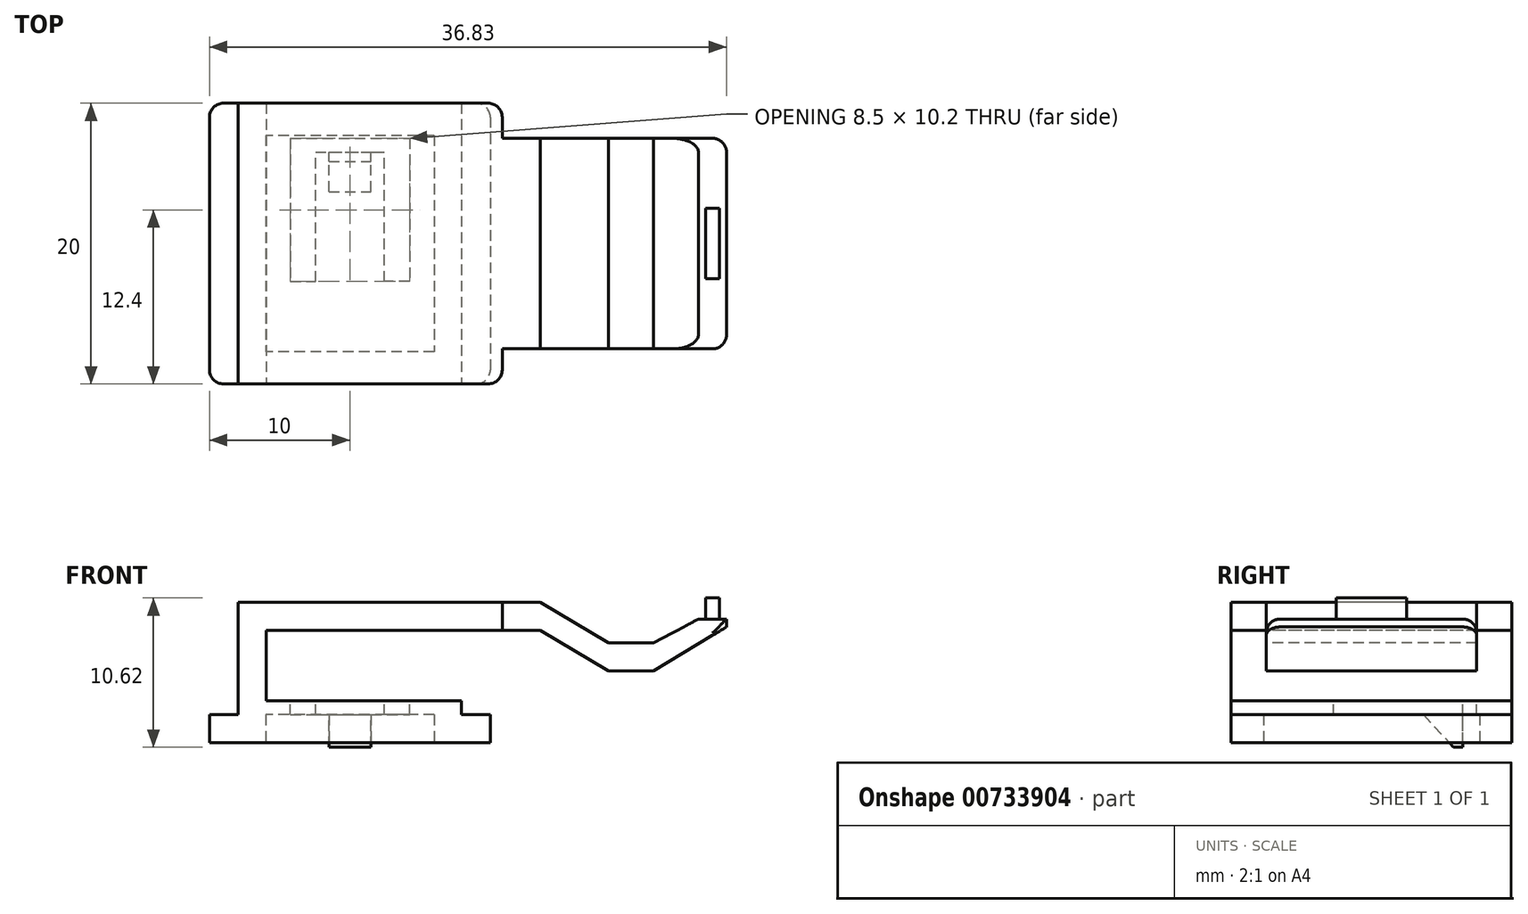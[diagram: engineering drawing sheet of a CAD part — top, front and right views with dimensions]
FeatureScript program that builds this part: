
annotation { "Feature Type Name" : "Feature", "Feature Type Description" : "" }
export const myFeature = defineFeature(function(context is Context, id is Id, definition is map)
    precondition{}
    {
        {
            var Q0;
            Q0=qCreatedBy(makeId("Top.planeOp"),FACE);
            var sketch = newSketch(context, id + "F0", { "sketchPlane" : qUnion([Q0])});
            skLineSegment(sketch, "E0.bottom", {"start": v(10, 10) * mm, "end": v(-10, 10) * mm});
            skLineSegment(sketch, "E0.top", {"start": v(10, -10) * mm, "end": v(-10, -10) * mm});
            skLineSegment(sketch, "E0.left", {"start": v(10, 10) * mm, "end": v(10, -10) * mm});
            skLineSegment(sketch, "E0.right", {"start": v(-10, 10) * mm, "end": v(-10, -10) * mm});
            skPoint(sketch, "E0.middle", {"position": v(0, 0) * mm});
            skLineSegment(sketch, "E1.bottom", {"start": v(6, 7.7) * mm, "end": v(-6, 7.7) * mm});
            skLineSegment(sketch, "E1.top", {"start": v(6, -7.7) * mm, "end": v(-6, -7.7) * mm});
            skLineSegment(sketch, "E1.left", {"start": v(6, 7.7) * mm, "end": v(6, -7.7) * mm});
            skLineSegment(sketch, "E1.right", {"start": v(-6, 7.7) * mm, "end": v(-6, -7.7) * mm});
            skSolve(sketch);
        }
        {
            var Q0;
            Q0 = qSketchRegion(id + "F0", true);
            extrude(context, id + "F1", {"entities" : qUnion([Q0]), "depth" : 2 * mm, "offsetDistance" : 25 * mm});
        }
        {
            var Q0;
            Q0=makeQuery(id+"F1.opExtrude","CAP_FACE",FACE,{"disambiguationData":[OSD([sQuery(id+"F0.wireOp",EDGE,"E0.bottom"),sQuery(id+"F0.wireOp",EDGE,"E0.top"),sQuery(id+"F0.wireOp",EDGE,"E0.left"),sQuery(id+"F0.wireOp",EDGE,"E0.right"),sQuery(id+"F0.wireOp",EDGE,"E1.bottom"),sQuery(id+"F0.wireOp",EDGE,"E1.top"),sQuery(id+"F0.wireOp",EDGE,"E1.left"),sQuery(id+"F0.wireOp",EDGE,"E1.right")])],"isStart":false});
            var sketch = newSketch(context, id + "F2", { "sketchPlane" : qUnion([Q0])});
            skLineSegment(sketch, "E2.bottom", {"start": v(7.95, 10) * mm, "end": v(-7.95, 10) * mm});
            skLineSegment(sketch, "E2.top", {"start": v(7.95, -10) * mm, "end": v(-7.95, -10) * mm});
            skLineSegment(sketch, "E2.left", {"start": v(7.95, 10) * mm, "end": v(7.95, -10) * mm});
            skLineSegment(sketch, "E2.right", {"start": v(-7.95, 10) * mm, "end": v(-7.95, -10) * mm});
            skPoint(sketch, "E2.middle", {"position": v(0, 0) * mm});
            skSolve(sketch);
        }
        {
            var Q0;
            Q0 = qSketchRegion(id + "F2", true);
            extrude(context, id + "F3", {"entities" : qUnion([Q0]), "operationType" : NewBodyOperationType.ADD, "depth" : 1 * mm, "offsetDistance" : 25 * mm});
        }
        {
            var Q0;
            Q0=makeQuery(id+"F3.opExtrude","CAP_FACE",FACE,{"disambiguationData":[OSD([sQuery(id+"F2.wireOp",EDGE,"E2.bottom"),sQuery(id+"F2.wireOp",EDGE,"E2.top"),sQuery(id+"F2.wireOp",EDGE,"E2.left"),sQuery(id+"F2.wireOp",EDGE,"E2.right")])],"isStart":false});
            var sketch = newSketch(context, id + "F4", { "sketchPlane" : qUnion([Q0])});
            skLineSegment(sketch, "E3.bottom", {"start": v(-7.95, 10) * mm, "end": v(-5.95, 10) * mm});
            skLineSegment(sketch, "E3.top", {"start": v(-7.95, -10) * mm, "end": v(-5.95, -10) * mm});
            skLineSegment(sketch, "E3.left", {"start": v(-7.95, 10) * mm, "end": v(-7.95, -10) * mm});
            skLineSegment(sketch, "E3.right", {"start": v(-5.95, 10) * mm, "end": v(-5.95, -10) * mm});
            skSolve(sketch);
        }
        {
            var Q0;
            Q0=makeQuery(id+"F4.imprint","IMPRINT",FACE,{"disambiguationData":[TD([[makeQuery(id+"F4.imprint","IMPRINT",EDGE,{"derivedFrom":sQuery(id+"F4.wireOp",EDGE,"E3.bottom")}),1.0]])]});
            extrude(context, id + "F5", {"entities" : qUnion([Q0]), "operationType" : NewBodyOperationType.ADD, "depth" : 7 * mm, "offsetDistance" : 25 * mm});
        }
        {
            var Q0;
            Q0=makeQuery(id+"F3.opExtrude","CAP_FACE",FACE,{"disambiguationData":[OSD([sQuery(id+"F2.wireOp",EDGE,"E2.bottom"),sQuery(id+"F2.wireOp",EDGE,"E2.top"),sQuery(id+"F2.wireOp",EDGE,"E2.left"),sQuery(id+"F2.wireOp",EDGE,"E2.right")])],"isStart":false});
            var sketch = newSketch(context, id + "F6", { "sketchPlane" : qUnion([Q0])});
            skLineSegment(sketch, "E4", {"start": v(-4.25, 7.5) * mm, "end": v(-4.25, -2.7) * mm});
            skLineSegment(sketch, "E5", {"start": v(0, 10) * mm, "end": v(0, -10) * mm, "construction": true});
            skPoint(sketch, "E5.startSnap0", {"position": v(1, 10) * mm});
            skLineSegment(sketch, "E6", {"start": v(-4.25, -2.7) * mm, "end": v(-2.45, -2.7) * mm});
            skLineSegment(sketch, "E7", {"start": v(-2.45, -2.7) * mm, "end": v(-2.45, 6.5) * mm});
            skLineSegment(sketch, "E8", {"start": v(-2.45, 6.5) * mm, "end": v(0, 6.5) * mm});
            skLineSegment(sketch, "E9", {"start": v(-4.25, 7.5) * mm, "end": v(0, 7.5) * mm});
            skLineSegment(sketch, "E10.MirrorCS", {"start": v(2.45, 6.5) * mm, "end": v(0, 6.5) * mm});
            skLineSegment(sketch, "E11.MirrorCS", {"start": v(4.25, 7.5) * mm, "end": v(0, 7.5) * mm});
            skLineSegment(sketch, "E12.MirrorCS", {"start": v(4.25, 7.5) * mm, "end": v(4.25, -2.7) * mm});
            skLineSegment(sketch, "E13.MirrorCS", {"start": v(2.45, -2.7) * mm, "end": v(2.45, 6.5) * mm});
            skLineSegment(sketch, "E14.MirrorCS", {"start": v(4.25, -2.7) * mm, "end": v(2.45, -2.7) * mm});
            skSolve(sketch);
        }
        {
            var Q0;
            Q0=makeQuery(id+"F6.imprint","IMPRINT",FACE,{"disambiguationData":[TD([[makeQuery(id+"F6.imprint","IMPRINT",EDGE,{"derivedFrom":sQuery(id+"F6.wireOp",EDGE,"E4")}),1.0]])]});
            extrude(context, id + "F7", {"entities" : qUnion([Q0]), "operationType" : NewBodyOperationType.REMOVE, "endBound" : BoundingType.THROUGH_ALL, "oppositeDirection" : true, "depth" : 25 * mm, "offsetDistance" : 25 * mm});
        }
        {
            var Q0;
            Q0=makeQuery(id+"F3.opExtrude","CAP_FACE",FACE,{"disambiguationData":[OSD([sQuery(id+"F2.wireOp",EDGE,"E2.bottom"),sQuery(id+"F2.wireOp",EDGE,"E2.top"),sQuery(id+"F2.wireOp",EDGE,"E2.left"),sQuery(id+"F2.wireOp",EDGE,"E2.right")])],"isStart":true});
            var sketch = newSketch(context, id + "F8", { "sketchPlane" : qUnion([Q0])});
            skLineSegment(sketch, "E15", {"start": v(0, -6.5) * mm, "end": v(0, 0) * mm, "construction": true});
            skLineSegment(sketch, "E16", {"start": v(0, -3.7) * mm, "end": v(1.5, -3.7) * mm});
            skLineSegment(sketch, "E17", {"start": v(1.5, -3.7) * mm, "end": v(1.5, -6.5) * mm});
            skLineSegment(sketch, "E18.MirrorCS", {"start": v(0, -3.7) * mm, "end": v(-1.5, -3.7) * mm});
            skLineSegment(sketch, "E19.MirrorCS", {"start": v(-1.5, -3.7) * mm, "end": v(-1.5, -6.5) * mm});
            skSolve(sketch);
        }
        {
            var Q0;
            Q0=makeQuery(id+"F8.imprint","IMPRINT",FACE,{"disambiguationData":[TD([[makeQuery(id+"F8.imprint","IMPRINT",EDGE,{"derivedFrom":sQuery(id+"F8.wireOp",EDGE,"E16")}),-1.0]])]});
            extrude(context, id + "F9", {"entities" : qUnion([Q0]), "operationType" : NewBodyOperationType.ADD, "depth" : 2.3 * mm, "offsetDistance" : 25 * mm});
        }
        {
            var Q0;
            Q0=makeQuery(id+"F9.opExtrude","SWEPT_FACE",FACE,{"disambiguationData":[OSD([sQuery(id+"F8.wireOp",EDGE,"E17")])]});
            var sketch = newSketch(context, id + "F10", { "sketchPlane" : qUnion([Q0])});
            skLineSegment(sketch, "E20", {"start": v(3.7, 2) * mm, "end": v(5.85, -0.3) * mm});
            skLineSegment(sketch, "E21", {"start": v(5.85, -0.3) * mm, "end": v(3.7, -0.3) * mm});
            skLineSegment(sketch, "E22", {"start": v(3.7, -0.3) * mm, "end": v(3.7, 2) * mm});
            skSolve(sketch);
        }
        {
            var Q0;
            Q0=makeQuery(id+"F10.imprint","IMPRINT",FACE,{"disambiguationData":[TD([[makeQuery(id+"F10.imprint","IMPRINT",EDGE,{"derivedFrom":sQuery(id+"F10.wireOp",EDGE,"E20")}),-1.0]])]});
            extrude(context, id + "F11", {"entities" : qUnion([Q0]), "operationType" : NewBodyOperationType.REMOVE, "oppositeDirection" : true, "depth" : 4 * mm, "offsetDistance" : 25 * mm});
        }
        {
            var Q0;
            Q0=makeQuery(id+"F5.opExtrude","SWEPT_FACE",FACE,{"disambiguationData":[OSD([sQuery(id+"F4.wireOp",EDGE,"E3.right")])]});
            var sketch = newSketch(context, id + "F12", { "sketchPlane" : qUnion([Q0])});
            skLineSegment(sketch, "E23.bottom", {"start": v(10, 10) * mm, "end": v(-10, 10) * mm});
            skLineSegment(sketch, "E23.top", {"start": v(10, 8) * mm, "end": v(-10, 8) * mm});
            skLineSegment(sketch, "E23.left", {"start": v(10, 10) * mm, "end": v(10, 8) * mm});
            skLineSegment(sketch, "E23.right", {"start": v(-10, 10) * mm, "end": v(-10, 8) * mm});
            skSolve(sketch);
        }
        {
            var Q0;
            Q0=makeQuery(id+"F12.imprint","IMPRINT",FACE,{"disambiguationData":[TD([[makeQuery(id+"F12.imprint","IMPRINT",EDGE,{"derivedFrom":sQuery(id+"F12.wireOp",EDGE,"E23.bottom")}),1.0]])]});
            extrude(context, id + "F13", {"entities" : qUnion([Q0]), "operationType" : NewBodyOperationType.ADD, "depth" : 16.8 * mm, "offsetDistance" : 25 * mm});
        }
        {
            var Q0;
            Q0=makeQuery(id+"F13.opExtrude","CAP_FACE",FACE,{"disambiguationData":[OSD([sQuery(id+"F12.wireOp",EDGE,"E23.bottom"),sQuery(id+"F12.wireOp",EDGE,"E23.top"),sQuery(id+"F12.wireOp",EDGE,"E23.left"),sQuery(id+"F12.wireOp",EDGE,"E23.right")])],"isStart":false});
            var sketch = newSketch(context, id + "F14", { "sketchPlane" : qUnion([Q0])});
            skPoint(sketch, "E24", {"position": v(0, 9) * mm});
            skLineSegment(sketch, "E25.bottom", {"start": v(7.5, 8) * mm, "end": v(-7.5, 8) * mm});
            skLineSegment(sketch, "E25.top", {"start": v(7.5, 10) * mm, "end": v(-7.5, 10) * mm});
            skLineSegment(sketch, "E25.left", {"start": v(7.5, 8) * mm, "end": v(7.5, 10) * mm});
            skLineSegment(sketch, "E25.right", {"start": v(-7.5, 8) * mm, "end": v(-7.5, 10) * mm});
            skSolve(sketch);
        }
        {
            var Q0;
            Q0=makeQuery(id+"F14.imprint","IMPRINT",FACE,{"disambiguationData":[TD([[makeQuery(id+"F14.imprint","IMPRINT",EDGE,{"derivedFrom":sQuery(id+"F14.wireOp",EDGE,"E25.bottom")}),-1.0]])]});
            extrude(context, id + "F15", {"entities" : qUnion([Q0]), "operationType" : NewBodyOperationType.ADD, "depth" : 2.7 * mm, "offsetDistance" : 25 * mm});
        }
        {
            var Q0;
            Q0=makeQuery(id+"F15.opExtrude","CAP_FACE",FACE,{"disambiguationData":[OSD([sQuery(id+"F14.wireOp",EDGE,"E25.bottom"),sQuery(id+"F14.wireOp",EDGE,"E25.top"),sQuery(id+"F14.wireOp",EDGE,"E25.left"),sQuery(id+"F14.wireOp",EDGE,"E25.right")])],"isStart":false});
            var sketch = newSketch(context, id + "F16", { "sketchPlane" : qUnion([Q0])});
            skLineSegment(sketch, "E26.bottom", {"start": v(7.5, 10) * mm, "end": v(-7.5, 10) * mm});
            skLineSegment(sketch, "E26.top", {"start": v(7.5, 5.12) * mm, "end": v(-7.5, 5.12) * mm});
            skLineSegment(sketch, "E26.left", {"start": v(7.5, 10) * mm, "end": v(7.5, 5.12) * mm});
            skLineSegment(sketch, "E26.right", {"start": v(-7.5, 10) * mm, "end": v(-7.5, 5.12) * mm});
            skSolve(sketch);
        }
        {
            var Q0;
            {var subQ0=sQuery(id+"F16.wireOp",EDGE,"E26.top");Q0=makeQuery(id+"F16.imprint","IMPRINT",FACE,{"disambiguationData":[TD([[makeQuery(id+"F16.imprint","IMPRINT",EDGE,{"derivedFrom":subQ0}),-1.0]])]});}
            var Q1;
            {var subQ0=sQuery(id+"F16.wireOp",EDGE,"E26.bottom");Q1=makeQuery(id+"F16.imprint","IMPRINT",FACE,{"disambiguationData":[TD([[makeQuery(id+"F16.imprint","IMPRINT",EDGE,{"derivedFrom":subQ0}),1.0]])]});}
            extrude(context, id + "F17", {"entities" : qUnion([Q0, Q1]), "operationType" : NewBodyOperationType.ADD, "depth" : 4.88 * mm, "offsetDistance" : 25 * mm});
        }
        {
            var Q0;
            Q0=makeQuery(id+"F17.boolean.opBoolean","MERGE",FACE,{"derivedFrom":[makeQuery(id+"F15.opExtrude","SWEPT_FACE",FACE,{"disambiguationData":[OSD([sQuery(id+"F14.wireOp",EDGE,"E25.right")])]}),makeQuery(id+"F17.opExtrude","SWEPT_FACE",FACE,{"disambiguationData":[OSD([sQuery(id+"F16.wireOp",EDGE,"E26.right")])]})]});
            var sketch = newSketch(context, id + "F18", { "sketchPlane" : qUnion([Q0])});
            skLineSegment(sketch, "E27", {"start": v(13.55, 8) * mm, "end": v(18.43, 5.12) * mm});
            skLineSegment(sketch, "E28", {"start": v(18.43, 5.12) * mm, "end": v(18.43, 7.12) * mm});
            skLineSegment(sketch, "E29", {"start": v(18.43, 7.12) * mm, "end": v(13.55, 10) * mm});
            skPoint(sketch, "E29.endSnap0", {"position": v(14.64, 10) * mm});
            skLineSegment(sketch, "E30", {"start": v(13.55, 10) * mm, "end": v(13.55, 8) * mm});
            skSolve(sketch);
        }
        {
            var Q0;
            {var subQ0=sQuery(id+"F18.wireOp",EDGE,"E29");Q0=makeQuery(id+"F18.imprint","IMPRINT",FACE,{"disambiguationData":[TD([[makeQuery(id+"F18.imprint","IMPRINT",EDGE,{"derivedFrom":subQ0}),-1.0]])]});}
            var Q1;
            Q1=makeQuery(id+"F18.imprint","IMPRINT",FACE,{"disambiguationData":[TD([[makeQuery(id+"F18.imprint","IMPRINT",EDGE,{"derivedFrom":sQuery(id+"F18.wireOp",EDGE,"E27")}),-1.0]])]});
            extrude(context, id + "F19", {"entities" : qUnion([Q0, Q1]), "operationType" : NewBodyOperationType.REMOVE, "endBound" : BoundingType.THROUGH_ALL, "oppositeDirection" : true, "depth" : 25 * mm, "offsetDistance" : 25 * mm});
        }
        {
            var Q0;
            Q0=makeQuery(id+"F17.opExtrude","CAP_FACE",FACE,{"disambiguationData":[OSD([sQuery(id+"F16.wireOp",EDGE,"E26.bottom"),sQuery(id+"F16.wireOp",EDGE,"E26.top"),sQuery(id+"F16.wireOp",EDGE,"E26.left"),sQuery(id+"F16.wireOp",EDGE,"E26.right")])],"isStart":false});
            var sketch = newSketch(context, id + "F20", { "sketchPlane" : qUnion([Q0])});
            skLineSegment(sketch, "E31.bottom", {"start": v(-7.5, 5.12) * mm, "end": v(7.5, 5.12) * mm});
            skLineSegment(sketch, "E31.top", {"start": v(-7.5, 8.82) * mm, "end": v(7.5, 8.82) * mm});
            skLineSegment(sketch, "E31.left", {"start": v(-7.5, 5.12) * mm, "end": v(-7.5, 8.82) * mm});
            skLineSegment(sketch, "E31.right", {"start": v(7.5, 5.12) * mm, "end": v(7.5, 8.82) * mm});
            skSolve(sketch);
        }
        {
            var Q0;
            {var subQ0=sQuery(id+"F20.wireOp",EDGE,"E31.top");Q0=makeQuery(id+"F20.imprint","IMPRINT",FACE,{"disambiguationData":[TD([[makeQuery(id+"F20.imprint","IMPRINT",EDGE,{"derivedFrom":subQ0}),-1.0]])]});}
            var Q1;
            {var subQ0=sQuery(id+"F20.wireOp",EDGE,"E31.bottom");Q1=makeQuery(id+"F20.imprint","IMPRINT",FACE,{"disambiguationData":[TD([[makeQuery(id+"F20.imprint","IMPRINT",EDGE,{"derivedFrom":subQ0}),-1.0]])]});}
            extrude(context, id + "F21", {"entities" : qUnion([Q0, Q1]), "operationType" : NewBodyOperationType.ADD, "depth" : 8.4 * mm, "offsetDistance" : 25 * mm});
        }
        {
            var Q0;
            Q0=makeQuery(id+"F21.boolean.opBoolean","MERGE",FACE,{"derivedFrom":[makeQuery(id+"F17.boolean.opBoolean","MERGE",FACE,{"derivedFrom":[makeQuery(id+"F15.opExtrude","SWEPT_FACE",FACE,{"disambiguationData":[OSD([sQuery(id+"F14.wireOp",EDGE,"E25.right")])]}),makeQuery(id+"F17.opExtrude","SWEPT_FACE",FACE,{"disambiguationData":[OSD([sQuery(id+"F16.wireOp",EDGE,"E26.right")])]})]}),makeQuery(id+"F21.opExtrude","SWEPT_FACE",FACE,{"disambiguationData":[OSD([sQuery(id+"F20.wireOp",EDGE,"E31.left")])]})]});
            var sketch = newSketch(context, id + "F22", { "sketchPlane" : qUnion([Q0])});
            skLineSegment(sketch, "E32", {"start": v(26.83, 8.82) * mm, "end": v(24.83, 8.82) * mm});
            skLineSegment(sketch, "E33", {"start": v(18.43, 7.12) * mm, "end": v(21.63, 7.12) * mm});
            skLineSegment(sketch, "E34", {"start": v(24.83, 8.82) * mm, "end": v(21.63, 7.12) * mm});
            skLineSegment(sketch, "E35", {"start": v(18.43, 5.12) * mm, "end": v(21.63, 5.12) * mm});
            skLineSegment(sketch, "E36", {"start": v(21.63, 5.12) * mm, "end": v(26.83, 8.26) * mm});
            skLineSegment(sketch, "E37", {"start": v(26.83, 8.26) * mm, "end": v(26.83, 8.82) * mm});
            skLineSegment(sketch, "E38", {"start": v(18.43, 7.12) * mm, "end": v(18.43, 5.12) * mm});
            skSolve(sketch);
        }
        {
            var Q0;
            Q0=makeQuery(id+"F22.imprint","IMPRINT",FACE,{"disambiguationData":[TD([[makeQuery(id+"F22.imprint","IMPRINT",EDGE,{"derivedFrom":sQuery(id+"F22.wireOp",EDGE,"E33")}),1.0]])]});
            var Q1;
            {var subQ0=sQuery(id+"F22.wireOp",EDGE,"E36");Q1=makeQuery(id+"F22.imprint","IMPRINT",FACE,{"disambiguationData":[TD([[makeQuery(id+"F22.imprint","IMPRINT",EDGE,{"derivedFrom":subQ0}),-1.0]])]});}
            extrude(context, id + "F23", {"entities" : qUnion([Q0, Q1]), "operationType" : NewBodyOperationType.REMOVE, "endBound" : BoundingType.THROUGH_ALL, "oppositeDirection" : true, "depth" : 25 * mm, "offsetDistance" : 25 * mm});
        }
        {
            var Q0;
            Q0=makeQuery(id+"F21.opExtrude","SWEPT_FACE",FACE,{"disambiguationData":[OSD([sQuery(id+"F20.wireOp",EDGE,"E31.top")])]});
            var sketch = newSketch(context, id + "F24", { "sketchPlane" : qUnion([Q0])});
            skPoint(sketch, "E39", {"position": v(25.83, 0) * mm});
            skLineSegment(sketch, "E40", {"start": v(24.83, 0) * mm, "end": v(26.83, 0) * mm, "construction": true});
            skLineSegment(sketch, "E41.bottom", {"start": v(26.33, 2.5) * mm, "end": v(25.33, 2.5) * mm});
            skLineSegment(sketch, "E41.top", {"start": v(26.33, -2.5) * mm, "end": v(25.33, -2.5) * mm});
            skLineSegment(sketch, "E41.left", {"start": v(26.33, 2.5) * mm, "end": v(26.33, -2.5) * mm});
            skLineSegment(sketch, "E41.right", {"start": v(25.33, 2.5) * mm, "end": v(25.33, -2.5) * mm});
            skSolve(sketch);
        }
        {
            var Q0;
            Q0 = qSketchRegion(id + "F24", true);
            extrude(context, id + "F25", {"entities" : qUnion([Q0]), "operationType" : NewBodyOperationType.ADD, "depth" : 1.5 * mm, "offsetDistance" : 25 * mm});
        }
        {
            var Q0;
            Q0=makeQuery(id+"F21.opExtrude","SWEPT_EDGE",EDGE,{"disambiguationData":[OSD([sQuery(id+"F20.wireOp",EDGE,"E31.top"),sQuery(id+"F20.wireOp",EDGE,"E31.left")])]});
            var Q1;
            Q1=makeQuery(id+"F21.opExtrude","SWEPT_EDGE",EDGE,{"disambiguationData":[OSD([sQuery(id+"F20.wireOp",EDGE,"E31.top"),sQuery(id+"F20.wireOp",EDGE,"E31.right")])]});
            var Q2;
            Q2=makeQuery(id+"F21.opExtrude","CAP_EDGE",EDGE,{"disambiguationData":[OSD([sQuery(id+"F20.wireOp",EDGE,"E31.left")])],"isStart":false});
            var Q3;
            Q3=makeQuery(id+"F21.opExtrude","CAP_EDGE",EDGE,{"disambiguationData":[OSD([sQuery(id+"F20.wireOp",EDGE,"E31.right")])],"isStart":false});
            fillet(context, id + "F26", {"entities" : qUnion([Q0, Q1, Q2, Q3]), "radius" : 1 * mm, "tangentPropagation" : true, "allowEdgeOverflow" : false});
        }
        {
            var Q0;
            Q0=makeQuery(id+"F1.opExtrude","SWEPT_EDGE",EDGE,{"disambiguationData":[OSD([sQuery(id+"F0.wireOp",EDGE,"E0.top"),sQuery(id+"F0.wireOp",EDGE,"E0.left")])]});
            var Q1;
            Q1=makeQuery(id+"F1.opExtrude","SWEPT_EDGE",EDGE,{"disambiguationData":[OSD([sQuery(id+"F0.wireOp",EDGE,"E0.top"),sQuery(id+"F0.wireOp",EDGE,"E0.right")])]});
            var Q2;
            Q2=makeQuery(id+"F1.opExtrude","SWEPT_EDGE",EDGE,{"disambiguationData":[OSD([sQuery(id+"F0.wireOp",EDGE,"E0.bottom"),sQuery(id+"F0.wireOp",EDGE,"E0.right")])]});
            var Q3;
            Q3=makeQuery(id+"F1.opExtrude","SWEPT_EDGE",EDGE,{"disambiguationData":[OSD([sQuery(id+"F0.wireOp",EDGE,"E0.bottom"),sQuery(id+"F0.wireOp",EDGE,"E0.left")])]});
            var Q4;
            Q4=makeQuery(id+"F13.opExtrude","CAP_EDGE",EDGE,{"disambiguationData":[OSD([sQuery(id+"F12.wireOp",EDGE,"E23.left")])],"isStart":false});
            var Q5;
            Q5=makeQuery(id+"F13.opExtrude","CAP_EDGE",EDGE,{"disambiguationData":[OSD([sQuery(id+"F12.wireOp",EDGE,"E23.right")])],"isStart":false});
            fillet(context, id + "F27", {"entities" : qUnion([Q0, Q1, Q2, Q3, Q4, Q5]), "radius" : 1 * mm, "tangentPropagation" : true, "allowEdgeOverflow" : false});
        }
    });
